# Revit family: IDJ6-60_CC08116
name_source: partatom
category: Aparatos eléctricos
revit_build: Autodesk Revit 2016 (Build: 20150220_1215(x64)
units: mm (PartAtom-declared; Revit-internal decimal feet)

## family parameters
Compartido = No
Corte con vacíos al cargar = No
Cota de conector redondo = Diámetro de uso
Mantener orientación de anotación = No
Número OmniClass = 23.80.00.00
Punto de cálculo de habitación = No
Se basa en plano de trabajo = No
Siempre vertical = Sí
Tipo de pieza = Caja de conexiones
Título OmniClass = Electric Power and Lighting

## types (1)
- IDJ6
    Bastidor frontal = Acero templado, pintado epoxi
    Caudal máx. = 24800 l/h
    Conexiones = 316L acero inox.
    Costo = 0 $
    Código de montaje = CC08116
    Descripción = INTERCAMBIADOR PLACAS DESMONTABLE
    Dimensiones máx. = 1430x920x320 mm
    Fabricante = SALVADOR ESCODA
    Imagen de tipo = IDJ6.jpg
    Juntas = Nitrilo
    Modelo = IDJ6-60 PLACAS
    Placas = 316L acero inox.
    Potencia = 480000 Kcal/h
    Presión máx. trabajo = 16 bar
    Temperatura máx. trabajo = 100 ºC
    URL = www.salvadorescoda.com
